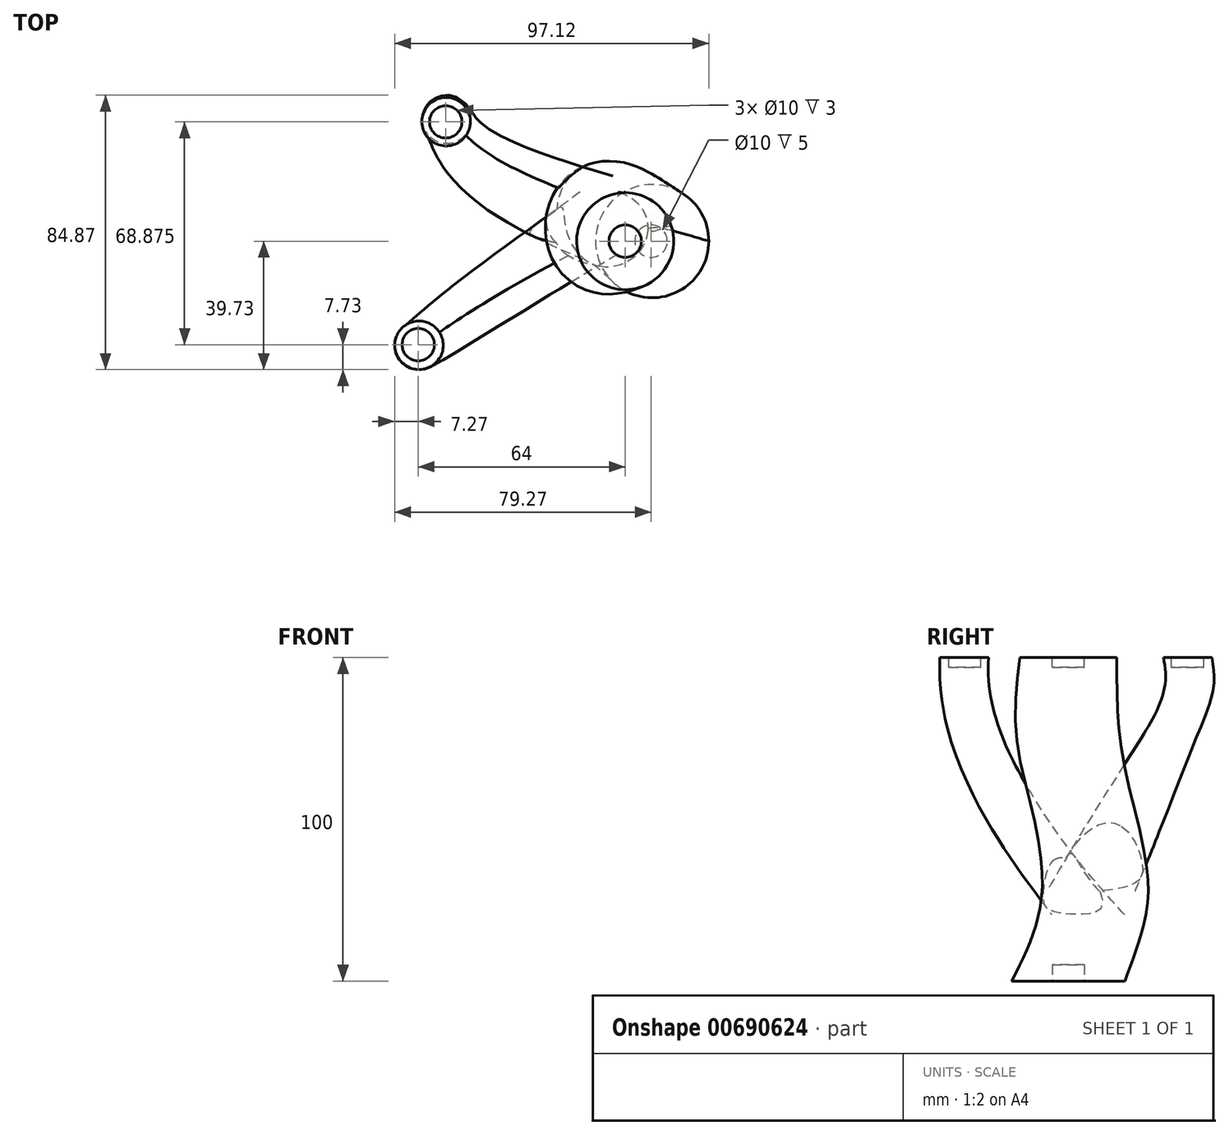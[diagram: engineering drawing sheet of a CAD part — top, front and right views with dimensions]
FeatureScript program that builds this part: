
annotation { "Feature Type Name" : "Feature", "Feature Type Description" : "" }
export const myFeature = defineFeature(function(context is Context, id is Id, definition is map)
    precondition{}
    {
        {
            var Q0;
            Q0=qCreatedBy(makeId("Top.planeOp"),FACE);
            var sketch = newSketch(context, id + "F0", { "sketchPlane" : qUnion([Q0])});
            skCircle(sketch, "E0", {"center": v(0, 0) * mm, "radius": 60 * mm, "construction": true});
            skCircle(sketch, "E1", {"center": v(-15.38, 36.93) * mm, "radius": 7.5 * mm});
            skCircle(sketch, "E2", {"center": v(-23.76, -32.18) * mm, "radius": 7.5 * mm});
            skCircle(sketch, "E3", {"center": v(40, 0) * mm, "radius": 15 * mm});
            skCircle(sketch, "E4", {"center": v(0, 0) * mm, "radius": 40 * mm, "construction": true});
            skSolve(sketch);
        }
        {
            var Q0;
            Q0=qCreatedBy(makeId("Top.planeOp"),FACE);
            cPlane(context, id + "F1", {"entities" : qUnion([Q0]), "cplaneType" : CPlaneType.OFFSET, "offset" : 100 * mm, "oppositeDirection" : true, "width" : 150 * mm, "height" : 150 * mm});
        }
        {
            var Q0;
            Q0=qCreatedBy(id+"F1.planeOp",FACE);
            var sketch = newSketch(context, id + "F2", { "sketchPlane" : qUnion([Q0])});
            skCircle(sketch, "E5", {"center": v(48.35, 0) * mm, "radius": 17.5 * mm});
            skSolve(sketch);
        }
        {
            var Q0;
            Q0=qCreatedBy(makeId("Top.planeOp"),FACE);
            cPlane(context, id + "F3", {"entities" : qUnion([Q0]), "cplaneType" : CPlaneType.OFFSET, "offset" : 25 * mm, "oppositeDirection" : true, "width" : 150 * mm, "height" : 150 * mm});
        }
        {
            var Q0;
            Q0=qCreatedBy(makeId("Top.planeOp"),FACE);
            cPlane(context, id + "F4", {"entities" : qUnion([Q0]), "cplaneType" : CPlaneType.OFFSET, "offset" : 75 * mm, "oppositeDirection" : true, "width" : 150 * mm, "height" : 150 * mm});
        }
        {
            var Q0;
            Q0=qCreatedBy(id+"F4.planeOp",FACE);
            var sketch = newSketch(context, id + "F5", { "sketchPlane" : qUnion([Q0])});
            skCircle(sketch, "E6", {"center": v(36.13, 8.14) * mm, "radius": 16.5 * mm});
            skSolve(sketch);
        }
        {
            var Q0;
            Q0=qCreatedBy(id+"F3.planeOp",FACE);
            var sketch = newSketch(context, id + "F6", { "sketchPlane" : qUnion([Q0])});
            skCircle(sketch, "E7", {"center": v(33.13, 0) * mm, "radius": 16 * mm});
            skSolve(sketch);
        }
        {
            var Q0;
            Q0=makeQuery(id+"F2.imprint","IMPRINT",FACE,{"disambiguationData":[TD([[makeQuery(id+"F2.imprint","IMPRINT",EDGE,{"derivedFrom":sQuery(id+"F2.wireOp",EDGE,"E5")}),1.0]])]});
            var Q1;
            Q1=makeQuery(id+"F5.imprint","IMPRINT",FACE,{"disambiguationData":[TD([[makeQuery(id+"F5.imprint","IMPRINT",EDGE,{"derivedFrom":sQuery(id+"F5.wireOp",EDGE,"E6")}),1.0]])]});
            var Q2;
            Q2=makeQuery(id+"F6.imprint","IMPRINT",FACE,{"disambiguationData":[TD([[makeQuery(id+"F6.imprint","IMPRINT",EDGE,{"derivedFrom":sQuery(id+"F6.wireOp",EDGE,"E7")}),1.0]])]});
            var Q3;
            Q3=makeQuery(id+"F0.imprint","IMPRINT",FACE,{"disambiguationData":[TD([[makeQuery(id+"F0.imprint","IMPRINT",EDGE,{"derivedFrom":sQuery(id+"F0.wireOp",EDGE,"E3")}),1.0]])]});
            loft(context, id + "F7", {"sheetProfilesArray" : [{ "sheetProfileEntities" : qUnion([Q0]) }, { "sheetProfileEntities" : qUnion([Q1]) }, { "sheetProfileEntities" : qUnion([Q2]) }, { "sheetProfileEntities" : qUnion([Q3]) }]});
        }
        {
            var Q0;
            Q0=qCreatedBy(id+"F4.planeOp",FACE);
            cPlane(context, id + "F8", {"entities" : qUnion([Q0]), "cplaneType" : CPlaneType.OFFSET, "offset" : 5 * mm, "width" : 150 * mm, "height" : 150 * mm});
        }
        {
            var Q0;
            Q0=qCreatedBy(id+"F4.planeOp",FACE);
            var sketch = newSketch(context, id + "F9", { "sketchPlane" : qUnion([Q0])});
            skCircle(sketch, "E8", {"center": v(35.98, 5.65) * mm, "radius": 13.89 * mm});
            skSolve(sketch);
        }
        {
            var Q0;
            Q0=qCreatedBy(id+"F3.planeOp",FACE);
            var sketch = newSketch(context, id + "F10", { "sketchPlane" : qUnion([Q0])});
            skCircle(sketch, "E9", {"center": v(-11.16, 31.01) * mm, "radius": 8.5 * mm});
            skSolve(sketch);
        }
        {
            var Q0;
            Q0=qCreatedBy(makeId("Top.planeOp"),FACE);
            cPlane(context, id + "F11", {"entities" : qUnion([Q0]), "cplaneType" : CPlaneType.OFFSET, "offset" : 5 * mm, "oppositeDirection" : true, "width" : 150 * mm, "height" : 150 * mm});
        }
        {
            var Q0;
            Q0=qCreatedBy(id+"F11.planeOp",FACE);
            var sketch = newSketch(context, id + "F12", { "sketchPlane" : qUnion([Q0])});
            skCircle(sketch, "E10", {"center": v(-23.72, -32.22) * mm, "radius": 7.5 * mm});
            skCircle(sketch, "E11", {"center": v(-15.2, 37.6) * mm, "radius": 7.5 * mm});
            skSolve(sketch);
        }
        {
            var Q1;
            Q1=makeQuery(id+"F9.imprint","IMPRINT",FACE,{"disambiguationData":[TD([[makeQuery(id+"F9.imprint","IMPRINT",EDGE,{"derivedFrom":sQuery(id+"F9.wireOp",EDGE,"E8")}),1.0]])]});
            var Q2;
            Q2=makeQuery(id+"F10.imprint","IMPRINT",FACE,{"disambiguationData":[TD([[makeQuery(id+"F10.imprint","IMPRINT",EDGE,{"derivedFrom":sQuery(id+"F10.wireOp",EDGE,"E9")}),1.0]])]});
            var Q3;
            Q3=makeQuery(id+"F12.imprint","IMPRINT",FACE,{"disambiguationData":[TD([[makeQuery(id+"F12.imprint","IMPRINT",EDGE,{"derivedFrom":sQuery(id+"F12.wireOp",EDGE,"E11")}),1.0]])]});
            var Q4;
            Q4=makeQuery(id+"F0.imprint","IMPRINT",FACE,{"disambiguationData":[TD([[makeQuery(id+"F0.imprint","IMPRINT",EDGE,{"derivedFrom":sQuery(id+"F0.wireOp",EDGE,"E1")}),1.0]])]});
            loft(context, id + "F13", {"operationType" : NewBodyOperationType.ADD, "sheetProfilesArray" : [{ "sheetProfileEntities" : qUnion([Q1]) }, { "sheetProfileEntities" : qUnion([Q2]) }, { "sheetProfileEntities" : qUnion([Q3]) }, { "sheetProfileEntities" : qUnion([Q4]) }]});
        }
        {
            var Q0;
            Q0=qCreatedBy(id+"F8.planeOp",FACE);
            cPlane(context, id + "F14", {"entities" : qUnion([Q0]), "cplaneType" : CPlaneType.OFFSET, "offset" : 12 * mm, "oppositeDirection" : true, "width" : 150 * mm, "height" : 150 * mm});
        }
        {
            var Q0;
            Q0=qCreatedBy(id+"F3.planeOp",FACE);
            cPlane(context, id + "F15", {"entities" : qUnion([Q0]), "cplaneType" : CPlaneType.OFFSET, "offset" : 15 * mm, "oppositeDirection" : true, "width" : 150 * mm, "height" : 150 * mm});
        }
        {
            var Q0;
            Q0=qCreatedBy(id+"F15.planeOp",FACE);
            var sketch = newSketch(context, id + "F16", { "sketchPlane" : qUnion([Q0])});
            skCircle(sketch, "E12", {"center": v(-8.7, -21.63) * mm, "radius": 9 * mm});
            skSolve(sketch);
        }
        {
            var Q0;
            Q0=qCreatedBy(id+"F14.planeOp",FACE);
            var sketch = newSketch(context, id + "F17", { "sketchPlane" : qUnion([Q0])});
            skCircle(sketch, "E13", {"center": v(35.95, 8.25) * mm, "radius": 11.5 * mm});
            skSolve(sketch);
        }
        {
            var Q1;
            Q1=makeQuery(id+"F17.imprint","IMPRINT",FACE,{"disambiguationData":[TD([[makeQuery(id+"F17.imprint","IMPRINT",EDGE,{"derivedFrom":sQuery(id+"F17.wireOp",EDGE,"E13")}),1.0]])]});
            var Q2;
            Q2=makeQuery(id+"F16.imprint","IMPRINT",FACE,{"disambiguationData":[TD([[makeQuery(id+"F16.imprint","IMPRINT",EDGE,{"derivedFrom":sQuery(id+"F16.wireOp",EDGE,"E12")}),1.0]])]});
            var Q3;
            Q3=makeQuery(id+"F12.imprint","IMPRINT",FACE,{"disambiguationData":[TD([[makeQuery(id+"F12.imprint","IMPRINT",EDGE,{"derivedFrom":sQuery(id+"F12.wireOp",EDGE,"E10")}),1.0]])]});
            var Q4;
            Q4=makeQuery(id+"F0.imprint","IMPRINT",FACE,{"disambiguationData":[TD([[makeQuery(id+"F0.imprint","IMPRINT",EDGE,{"derivedFrom":sQuery(id+"F0.wireOp",EDGE,"E2")}),1.0]])]});
            loft(context, id + "F18", {"operationType" : NewBodyOperationType.ADD, "sheetProfilesArray" : [{ "sheetProfileEntities" : qUnion([Q1]) }, { "sheetProfileEntities" : qUnion([Q2]) }, { "sheetProfileEntities" : qUnion([Q3]) }, { "sheetProfileEntities" : qUnion([Q4]) }]});
        }
        {
            var Q0;
            Q0=qCreatedBy(makeId("Top.planeOp"),FACE);
            var sketch = newSketch(context, id + "F19", { "sketchPlane" : qUnion([Q0])});
            skCircle(sketch, "E14", {"center": v(40, 0) * mm, "radius": 5 * mm});
            skCircle(sketch, "E15", {"center": v(-15.5, 36.87) * mm, "radius": 5 * mm});
            skCircle(sketch, "E16", {"center": v(-24, -32) * mm, "radius": 5 * mm});
            skCircle(sketch, "E17", {"center": v(0, 0) * mm, "radius": 40 * mm, "construction": true});
            skSolve(sketch);
        }
        {
            var Q0;
            Q0=makeQuery(id+"F19.imprint","IMPRINT",FACE,{"disambiguationData":[TD([[makeQuery(id+"F19.imprint","IMPRINT",EDGE,{"derivedFrom":sQuery(id+"F19.wireOp",EDGE,"E16")}),1.0]])]});
            var Q1;
            Q1=makeQuery(id+"F19.imprint","IMPRINT",FACE,{"disambiguationData":[TD([[makeQuery(id+"F19.imprint","IMPRINT",EDGE,{"derivedFrom":sQuery(id+"F19.wireOp",EDGE,"E15")}),1.0]])]});
            var Q2;
            Q2=makeQuery(id+"F19.imprint","IMPRINT",FACE,{"disambiguationData":[TD([[makeQuery(id+"F19.imprint","IMPRINT",EDGE,{"derivedFrom":sQuery(id+"F19.wireOp",EDGE,"E14")}),1.0]])]});
            extrude(context, id + "F20", {"entities" : qUnion([Q0, Q1, Q2]), "operationType" : NewBodyOperationType.REMOVE, "oppositeDirection" : true, "depth" : 3 * mm, "offsetDistance" : 25 * mm});
        }
        {
            var Q0;
            Q0=makeQuery(id+"F7.opLoft","CAP_FACE",FACE,{"disambiguationData":[OSD([makeQuery(id+"F2.imprint","IMPRINT",FACE,{"disambiguationData":[TD([[makeQuery(id+"F2.imprint","IMPRINT",EDGE,{"derivedFrom":sQuery(id+"F2.wireOp",EDGE,"E5")}),1.0]])]})])],"isStart":true});
            var sketch = newSketch(context, id + "F21", { "sketchPlane" : qUnion([Q0])});
            skCircle(sketch, "E18", {"center": v(48, 0) * mm, "radius": 5 * mm});
            skSolve(sketch);
        }
        {
            var Q0;
            Q0 = qSketchRegion(id + "F21", true);
            extrude(context, id + "F22", {"entities" : qUnion([Q0]), "operationType" : NewBodyOperationType.REMOVE, "oppositeDirection" : true, "depth" : 5 * mm, "offsetDistance" : 25 * mm});
        }
    });
